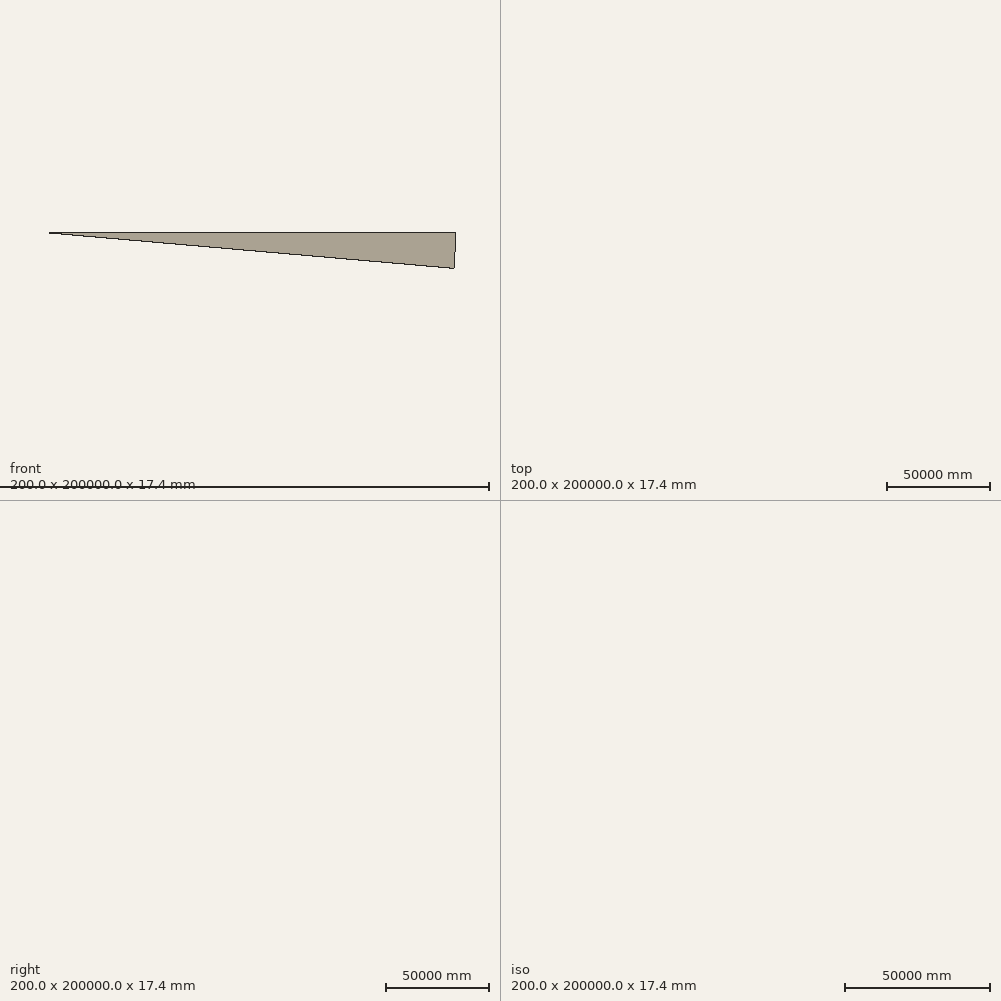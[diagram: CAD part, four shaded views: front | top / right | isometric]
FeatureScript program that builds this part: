
annotation { "Feature Type Name" : "Feature", "Feature Type Description" : "" }
export const myFeature = defineFeature(function(context is Context, id is Id, definition is map)
    precondition{}
    {
        {
            var Q0;
            Q0=qCreatedBy(makeId("Front.planeOp"),FACE);
            var sketch = newSketch(context, id + "F0", { "sketchPlane" : qUnion([Q0])});
            skCircle(sketch, "E0", {"center": v(0, 0) * mm, "radius": 200 * mm});
            skLineSegment(sketch, "E1", {"start": v(0, 0) * mm, "end": v(199.24, -17.43) * mm});
            skLineSegment(sketch, "E2", {"start": v(0, 0) * mm, "end": v(200, 0) * mm});
            skSolve(sketch);
        }
        {
            var Q0;
            {var subQ0=sQuery(id+"F0.wireOp",EDGE,"E1");Q0=makeQuery(id+"F0.imprint","IMPRINT",FACE,{"disambiguationData":[TD([[makeQuery(id+"F0.imprint","IMPRINT",EDGE,{"derivedFrom":subQ0}),1.0]])]});}
            extrude(context, id + "F1", {"entities" : qUnion([Q0]), "endBound" : BoundingType.SYMMETRIC, "depth" : 200000 * mm});
        }
    });
